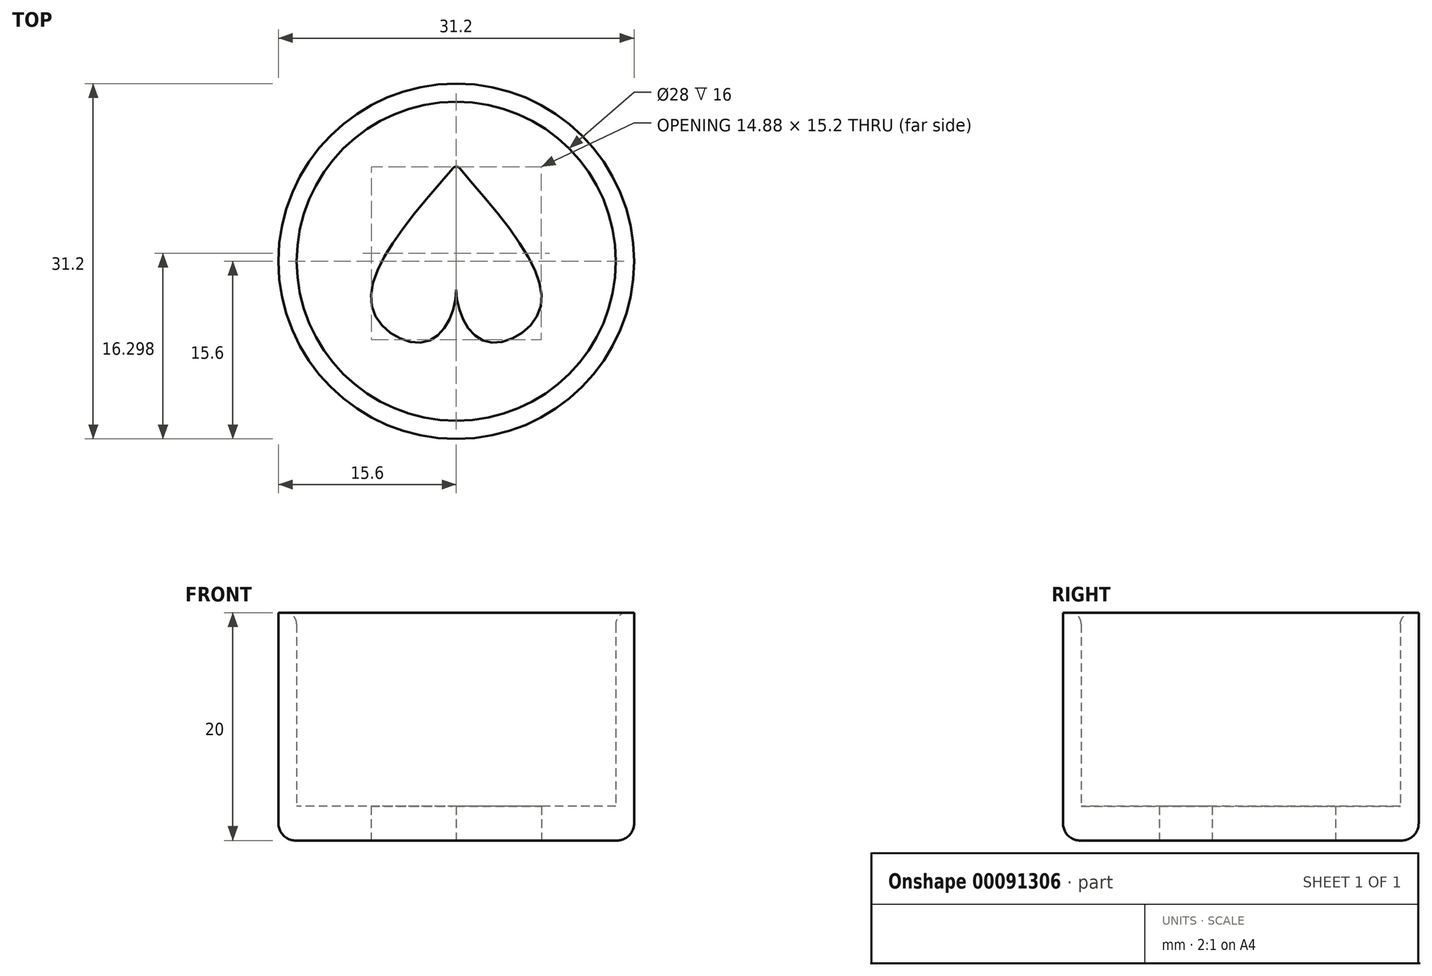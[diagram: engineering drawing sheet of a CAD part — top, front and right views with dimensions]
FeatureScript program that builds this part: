
annotation { "Feature Type Name" : "Feature", "Feature Type Description" : "" }
export const myFeature = defineFeature(function(context is Context, id is Id, definition is map)
    precondition{}
    {
        {
            var Q0;
            Q0=qCreatedBy(makeId("Top.planeOp"),FACE);
            var sketch = newSketch(context, id + "F0", { "sketchPlane" : qUnion([Q0])});
            skCircle(sketch, "E0", {"center": v(0, 0) * mm, "radius": 15.6 * mm});
            skCircle(sketch, "E1", {"center": v(0, 0) * mm, "radius": 14 * mm});
            skCircle(sketch, "E2", {"center": v(0, 0) * mm, "radius": 2 * mm});
            skSolve(sketch);
        }
        {
            var Q0;
            Q0=makeQuery(id+"F0.imprint","IMPRINT",FACE,{"disambiguationData":[TD([[makeQuery(id+"F0.imprint","IMPRINT",EDGE,{"derivedFrom":sQuery(id+"F0.wireOp",EDGE,"E1")}),1.0]])]});
            var Q1;
            Q1=makeQuery(id+"F0.imprint","IMPRINT",FACE,{"disambiguationData":[TD([[makeQuery(id+"F0.imprint","IMPRINT",EDGE,{"derivedFrom":sQuery(id+"F0.wireOp",EDGE,"E0")}),1.0]])]});
            var Q2;
            Q2=makeQuery(id+"F0.imprint","IMPRINT",FACE,{"disambiguationData":[TD([[makeQuery(id+"F0.imprint","IMPRINT",EDGE,{"derivedFrom":sQuery(id+"F0.wireOp",EDGE,"E2")}),1.0]])]});
            extrude(context, id + "F1", {"entities" : qUnion([Q0, Q1, Q2]), "depth" : 3 * mm});
        }
        {
            var Q0;
            Q0=makeQuery(id+"F0.imprint","IMPRINT",FACE,{"disambiguationData":[TD([[makeQuery(id+"F0.imprint","IMPRINT",EDGE,{"derivedFrom":sQuery(id+"F0.wireOp",EDGE,"E0")}),1.0]])]});
            extrude(context, id + "F2", {"entities" : qUnion([Q0]), "operationType" : NewBodyOperationType.ADD, "depth" : 20 * mm});
        }
        {
            var Q0;
            Q0=makeQuery(id+"F1.opExtrude","CAP_EDGE",EDGE,{"disambiguationData":[OSD([sQuery(id+"F0.wireOp",EDGE,"E0")])],"isStart":true});
            fillet(context, id + "F3", {"entities" : qUnion([Q0]), "radius" : 1.5 * mm, "tangentPropagation" : true, "allowEdgeOverflow" : false});
        }
        {
            var Q0;
            Q0=makeQuery(id+"F2.opExtrude","CAP_EDGE",EDGE,{"disambiguationData":[OSD([sQuery(id+"F0.wireOp",EDGE,"E1")])],"isStart":false});
            fillet(context, id + "F4", {"entities" : qUnion([Q0]), "radius" : 1 * mm, "tangentPropagation" : true, "allowEdgeOverflow" : false});
        }
        {
            var Q0;
            Q0=makeQuery(id+"F0.imprint","IMPRINT",FACE,{"disambiguationData":[TD([[makeQuery(id+"F0.imprint","IMPRINT",EDGE,{"derivedFrom":sQuery(id+"F0.wireOp",EDGE,"E1")}),1.0]])]});
            var sketch = newSketch(context, id + "F5", { "sketchPlane" : qUnion([Q0])});
            skFitSpline(sketch, "E3", {"points": [v(0, -2.51) * mm, v(-2.51, -7.02) * mm, v(-7.35, -4.16) * mm, v(0, 8.51) * mm], "startDerivative": vector(0, -18.26) * mm, "endDerivative": vector(27.13, 31.48) * mm});
            skLineSegment(sketch, "E4", {"start": v(0, -2.51) * mm, "end": v(0, 8.51) * mm, "construction": true});
            skFitSpline(sketch, "E5.MirrorCS", {"points": [v(0, -2.51) * mm, v(2.51, -7.02) * mm, v(7.35, -4.16) * mm, v(0, 8.51) * mm], "startDerivative": vector(0, -18.26) * mm, "endDerivative": vector(-27.13, 31.48) * mm});
            skSolve(sketch);
        }
        {
            var Q0;
            Q0=makeQuery(id+"F5.imprint","IMPRINT",FACE,{"disambiguationData":[TD([[makeQuery(id+"F5.imprint","IMPRINT",EDGE,{"derivedFrom":sQuery(id+"F5.wireOp",EDGE,"E3")}),-1.0]])]});
            var Q1;
            Q1=makeQuery(id+"F0.imprint","IMPRINT",FACE,{"disambiguationData":[TD([[makeQuery(id+"F0.imprint","IMPRINT",EDGE,{"derivedFrom":sQuery(id+"F0.wireOp",EDGE,"E2")}),1.0]])]});
            extrude(context, id + "F6", {"entities" : qUnion([Q0, Q1]), "operationType" : NewBodyOperationType.REMOVE, "endBound" : BoundingType.UP_TO_NEXT, "depth" : 25 * mm});
        }
        {
            var Q0;
            {var subQ0=sQuery(id+"F5.wireOp",EDGE,"E5.MirrorCS");var subQ1=sQuery(id+"F5.wireOp",EDGE,"E3");Q0=makeQuery(id+"F6.boolean.opBoolean","COPY",EDGE,{"derivedFrom":makeQuery(id+"F6.opExtrude","SWEPT_EDGE",EDGE,{"disambiguationData":[OSD([subQ1,subQ0]),TDD([makeQuery(id+"F5.imprint","INTERSECT",VERTEX,{"disambiguationData":[OD(0.0)],"derivedFrom":[subQ1,subQ0]})])]})});}
            fillet(context, id + "F7", {"entities" : qUnion([Q0]), "radius" : 0.4 * mm, "tangentPropagation" : true, "allowEdgeOverflow" : false});
        }
    });
